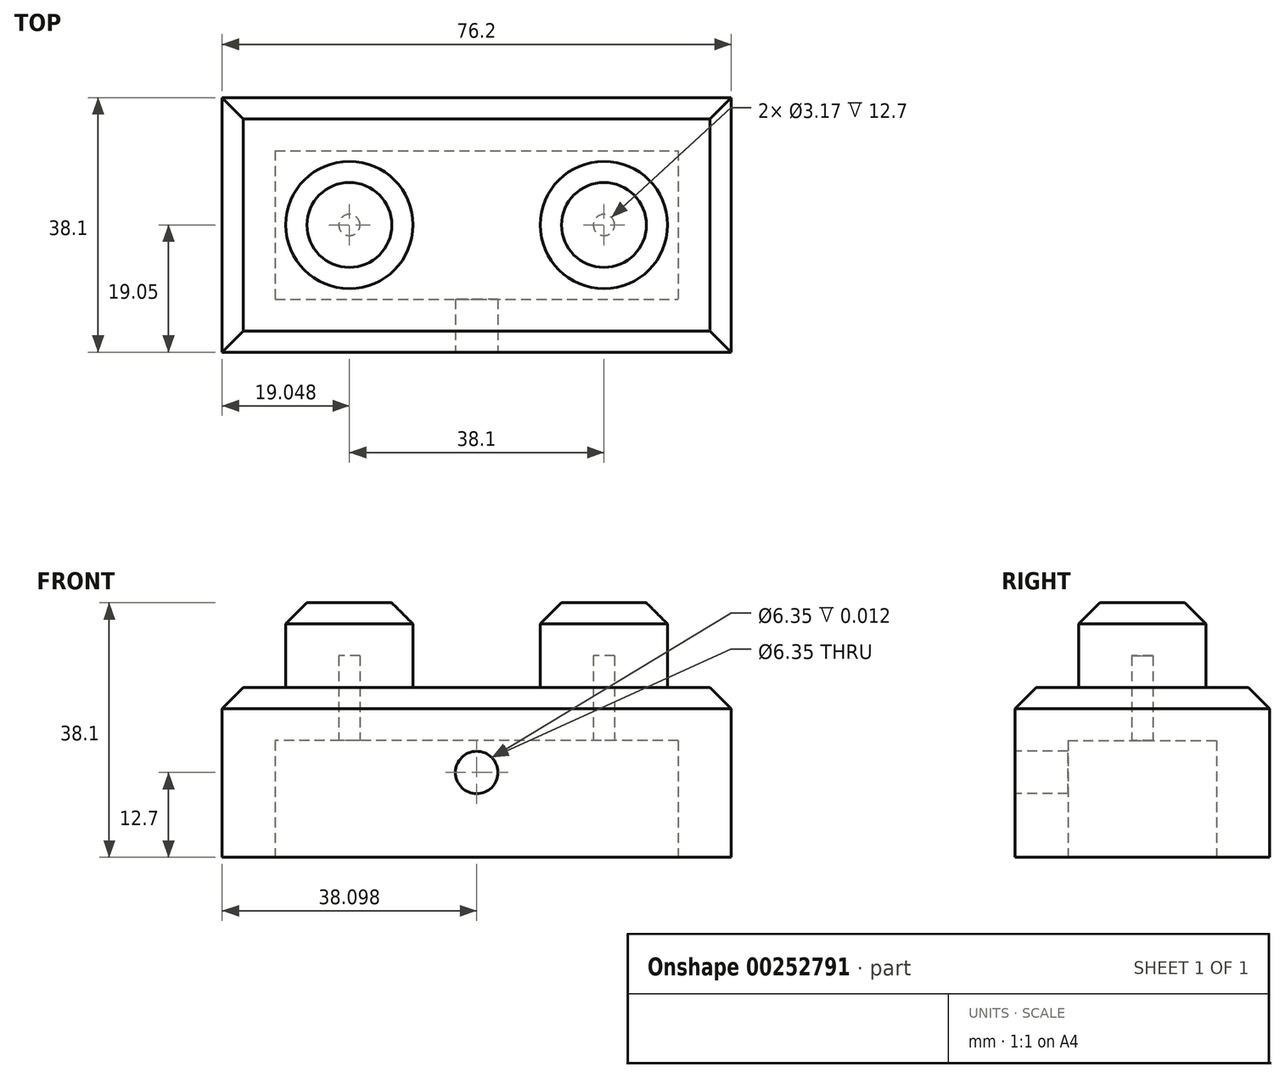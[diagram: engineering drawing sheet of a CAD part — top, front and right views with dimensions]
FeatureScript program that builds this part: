
annotation { "Feature Type Name" : "Feature", "Feature Type Description" : "" }
export const myFeature = defineFeature(function(context is Context, id is Id, definition is map)
    precondition{}
    {
        {
            var Q0;
            Q0=qCreatedBy(makeId("Top.planeOp"),FACE);
            var sketch = newSketch(context, id + "F0", { "sketchPlane" : qUnion([Q0])});
            skLineSegment(sketch, "E0.bottom", {"start": v(31.67, -12.8) * mm, "end": v(107.87, -12.8) * mm});
            skLineSegment(sketch, "E0.top", {"start": v(31.67, -50.9) * mm, "end": v(107.87, -50.9) * mm});
            skLineSegment(sketch, "E0.left", {"start": v(31.67, -12.8) * mm, "end": v(31.67, -50.9) * mm});
            skLineSegment(sketch, "E0.right", {"start": v(107.87, -12.8) * mm, "end": v(107.87, -50.9) * mm});
            skSolve(sketch);
        }
        {
            var Q0;
            Q0 = qSketchRegion(id + "F0", true);
            extrude(context, id + "F1", {"entities" : qUnion([Q0]), "depth" : 25.4 * mm});
        }
        {
            var Q0;
            Q0=makeQuery(id+"F1.opExtrude","CAP_FACE",FACE,{"disambiguationData":[OSD([sQuery(id+"F0.wireOp",EDGE,"E0.bottom"),sQuery(id+"F0.wireOp",EDGE,"E0.top"),sQuery(id+"F0.wireOp",EDGE,"E0.left"),sQuery(id+"F0.wireOp",EDGE,"E0.right")])],"isStart":false});
            var sketch = newSketch(context, id + "F2", { "sketchPlane" : qUnion([Q0])});
            skCircle(sketch, "E1", {"center": v(88.82, -31.84) * mm, "radius": 9.53 * mm});
            skCircle(sketch, "E2", {"center": v(50.72, -31.84) * mm, "radius": 9.53 * mm});
            skSolve(sketch);
        }
        {
            var Q0;
            Q0 = qSketchRegion(id + "F2", true);
            extrude(context, id + "F3", {"entities" : qUnion([Q0]), "operationType" : NewBodyOperationType.ADD, "depth" : 12.7 * mm});
        }
        {
            var Q0;
            Q0=makeQuery(id+"F3.opExtrude","CAP_EDGE",EDGE,{"disambiguationData":[OSD([sQuery(id+"F2.wireOp",EDGE,"E2")])],"isStart":false});
            var Q1;
            Q1=makeQuery(id+"F3.opExtrude","CAP_EDGE",EDGE,{"disambiguationData":[OSD([sQuery(id+"F2.wireOp",EDGE,"E1")])],"isStart":false});
            var Q2;
            Q2=makeQuery(id+"F1.opExtrude","CAP_EDGE",EDGE,{"disambiguationData":[OSD([sQuery(id+"F0.wireOp",EDGE,"E0.top")])],"isStart":false});
            var Q3;
            Q3=makeQuery(id+"F1.opExtrude","CAP_EDGE",EDGE,{"disambiguationData":[OSD([sQuery(id+"F0.wireOp",EDGE,"E0.left")])],"isStart":false});
            var Q4;
            Q4=makeQuery(id+"F1.opExtrude","CAP_EDGE",EDGE,{"disambiguationData":[OSD([sQuery(id+"F0.wireOp",EDGE,"E0.right")])],"isStart":false});
            var Q5;
            Q5=makeQuery(id+"F1.opExtrude","CAP_EDGE",EDGE,{"disambiguationData":[OSD([sQuery(id+"F0.wireOp",EDGE,"E0.bottom")])],"isStart":false});
            chamfer(context, id + "F4", {"entities" : qUnion([Q0, Q1, Q2, Q3, Q4, Q5]), "width" : 3.17 * mm, "tangentPropagation" : true});
        }
        {
            var Q0;
            Q0=makeQuery(id+"F1.opExtrude","CAP_FACE",FACE,{"disambiguationData":[OSD([sQuery(id+"F0.wireOp",EDGE,"E0.bottom"),sQuery(id+"F0.wireOp",EDGE,"E0.top"),sQuery(id+"F0.wireOp",EDGE,"E0.left"),sQuery(id+"F0.wireOp",EDGE,"E0.right")])],"isStart":true});
            shell(context, id + "F5", {"entities" : qUnion([Q0]), "thickness" : 7.94 * mm});
        }
        {
            var Q0;
            Q0=makeQuery(id+"F1.opExtrude","SWEPT_FACE",FACE,{"disambiguationData":[OSD([sQuery(id+"F0.wireOp",EDGE,"E0.bottom")])]});
            var sketch = newSketch(context, id + "F6", { "sketchPlane" : qUnion([Q0])});
            skCircle(sketch, "E3", {"center": v(-69.77, 12.7) * mm, "radius": 3.18 * mm});
            skSolve(sketch);
        }
        {
            var Q0;
            Q0 = qSketchRegion(id + "F6", true);
            extrude(context, id + "F7", {"entities" : qUnion([Q0]), "operationType" : NewBodyOperationType.REMOVE, "oppositeDirection" : true, "depth" : 5 / 406.4 * mm});
        }
        {
            var Q0;
            Q0=makeQuery(id+"F1.opExtrude","SWEPT_FACE",FACE,{"disambiguationData":[OSD([sQuery(id+"F0.wireOp",EDGE,"E0.top")])]});
            var sketch = newSketch(context, id + "F8", { "sketchPlane" : qUnion([Q0])});
            skCircle(sketch, "E4", {"center": v(69.77, 12.7) * mm, "radius": 3.18 * mm});
            skSolve(sketch);
        }
        {
            var Q0;
            Q0=makeQuery(id+"F8.imprint","IMPRINT",FACE,{"disambiguationData":[TD([[makeQuery(id+"F8.imprint","IMPRINT",EDGE,{"derivedFrom":sQuery(id+"F8.wireOp",EDGE,"E4")}),1.0]])]});
            var Q1;
            Q1=sQuery(id+"F8.wireOp",EDGE,"E4");
            extrude(context, id + "F9", {"entities" : qUnion([Q0]), "operationType" : NewBodyOperationType.REMOVE, "surfaceEntities" : qUnion([Q1]), "oppositeDirection" : true, "depth" : 7.94 * mm});
        }
    });
